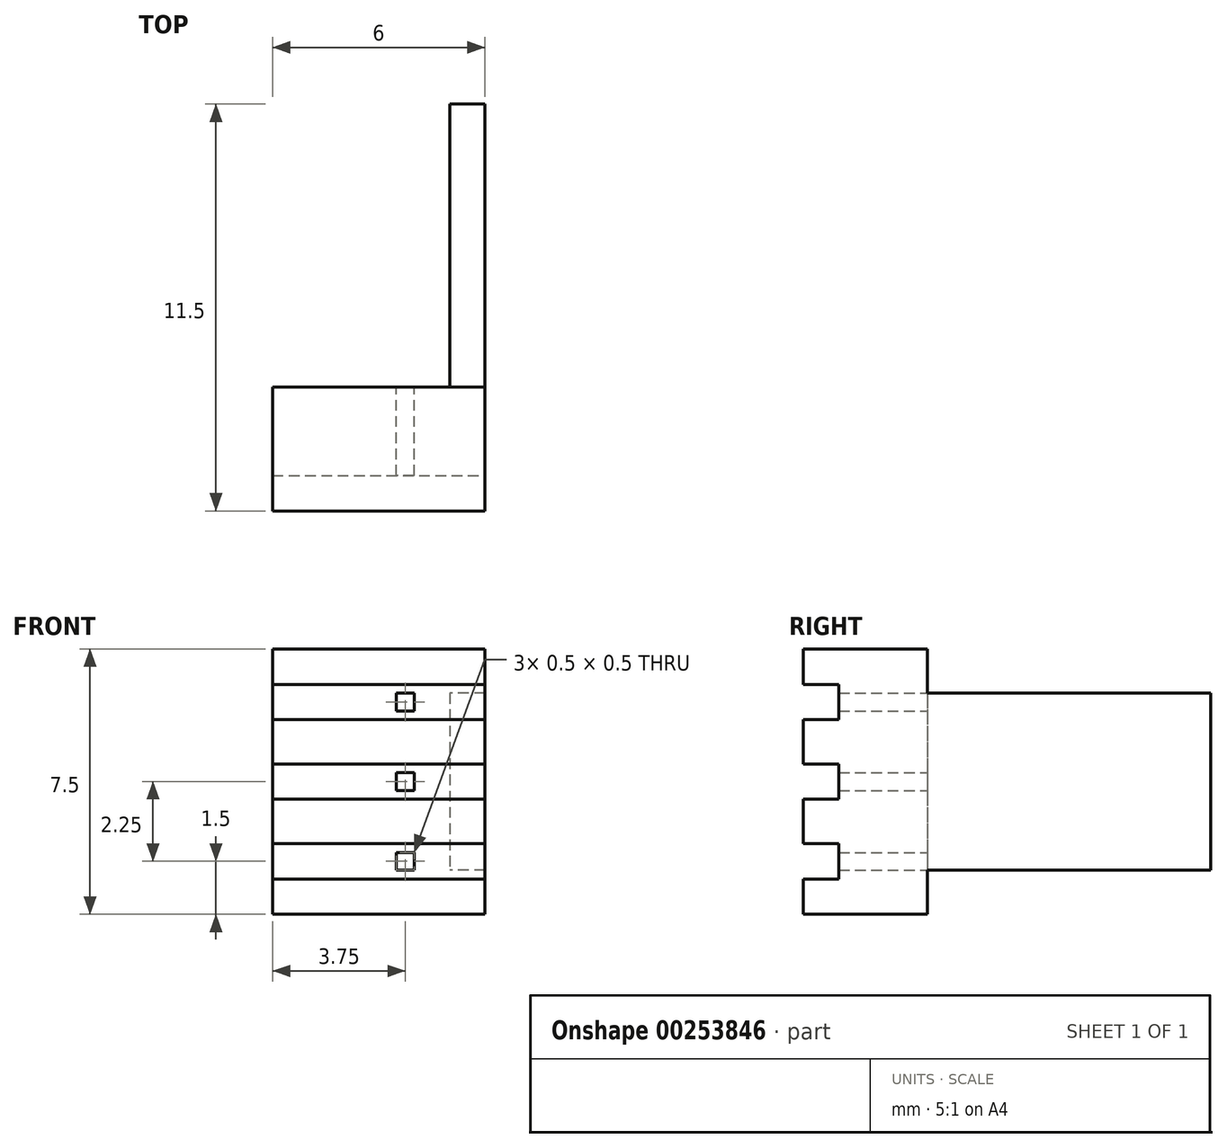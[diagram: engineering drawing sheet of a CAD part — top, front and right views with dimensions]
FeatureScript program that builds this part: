
annotation { "Feature Type Name" : "Feature", "Feature Type Description" : "" }
export const myFeature = defineFeature(function(context is Context, id is Id, definition is map)
    precondition{}
    {
        {
            var Q0;
            Q0=qCreatedBy(makeId("Top.planeOp"),FACE);
            var sketch = newSketch(context, id + "F0", { "sketchPlane" : qUnion([Q0])});
            skLineSegment(sketch, "E0.bottom", {"start": v(0, 0) * mm, "end": v(6, 0) * mm});
            skLineSegment(sketch, "E0.top", {"start": v(5, 11.5) * mm, "end": v(6, 11.5) * mm});
            skLineSegment(sketch, "E0.left", {"start": v(0, 0) * mm, "end": v(0, 3.5) * mm});
            skLineSegment(sketch, "E0.right", {"start": v(6, 0) * mm, "end": v(6, 11.5) * mm});
            skLineSegment(sketch, "E1", {"start": v(5, 11.5) * mm, "end": v(5, 3.5) * mm});
            skLineSegment(sketch, "E2", {"start": v(5, 3.5) * mm, "end": v(0, 3.5) * mm});
            skSolve(sketch);
        }
        {
            var Q0;
            Q0=qSketchRegion(id+"F0",true);
            extrude(context, id + "F1", {"entities" : qUnion([Q0]), "depth" : 7.5 * mm});
        }
        {
            var Q0;
            Q0=makeQuery(id+"F1.opExtrude","SWEPT_FACE",FACE,{"disambiguationData":[OSD([sQuery(id+"F0.wireOp",EDGE,"E1")])]});
            var sketch = newSketch(context, id + "F2", { "sketchPlane" : qUnion([Q0])});
            skLineSegment(sketch, "E3.bottom", {"start": v(-11.5, 0) * mm, "end": v(-3.5, 0) * mm});
            skLineSegment(sketch, "E3.top", {"start": v(-11.5, 1.25) * mm, "end": v(-3.5, 1.25) * mm});
            skLineSegment(sketch, "E3.left", {"start": v(-11.5, 0) * mm, "end": v(-11.5, 1.25) * mm});
            skLineSegment(sketch, "E3.right", {"start": v(-3.5, 0) * mm, "end": v(-3.5, 1.25) * mm});
            skLineSegment(sketch, "E4.bottom", {"start": v(-11.5, 7.5) * mm, "end": v(-3.5, 7.5) * mm});
            skLineSegment(sketch, "E4.top", {"start": v(-11.5, 6.25) * mm, "end": v(-3.5, 6.25) * mm});
            skLineSegment(sketch, "E4.left", {"start": v(-11.5, 7.5) * mm, "end": v(-11.5, 6.25) * mm});
            skLineSegment(sketch, "E4.right", {"start": v(-3.5, 7.5) * mm, "end": v(-3.5, 6.25) * mm});
            skSolve(sketch);
        }
        {
            var Q0;
            Q0=qSketchRegion(id+"F2",true);
            extrude(context, id + "F3", {"entities" : qUnion([Q0]), "operationType" : NewBodyOperationType.REMOVE, "oppositeDirection" : true, "depth" : 25 * mm});
        }
        {
            var Q0;
            Q0=makeQuery(id+"F3.boolean.opBoolean","MERGE",FACE,{"derivedFrom":[makeQuery(id+"F1.opExtrude","SWEPT_FACE",FACE,{"disambiguationData":[OSD([sQuery(id+"F0.wireOp",EDGE,"E2")])]}),makeQuery(id+"F3.opExtrude","SWEPT_FACE",FACE,{"disambiguationData":[OSD([sQuery(id+"F2.wireOp",EDGE,"E3.right")])]}),makeQuery(id+"F3.opExtrude","SWEPT_FACE",FACE,{"disambiguationData":[OSD([sQuery(id+"F2.wireOp",EDGE,"E4.right")])]})]});
            var sketch = newSketch(context, id + "F4", { "sketchPlane" : qUnion([Q0])});
            skLineSegment(sketch, "E5.bottom", {"start": v(-4, 6.25) * mm, "end": v(-3.5, 6.25) * mm});
            skLineSegment(sketch, "E5.top", {"start": v(-4, 1.25) * mm, "end": v(-3.5, 1.25) * mm});
            skLineSegment(sketch, "E5.left", {"start": v(-4, 6.25) * mm, "end": v(-4, 5.75) * mm});
            skLineSegment(sketch, "E5.right", {"start": v(-3.5, 6.25) * mm, "end": v(-3.5, 5.75) * mm});
            skLineSegment(sketch, "E6", {"start": v(-4, 5.75) * mm, "end": v(-3.5, 5.75) * mm});
            skLineSegment(sketch, "E7", {"start": v(-4, 1.75) * mm, "end": v(-3.5, 1.75) * mm});
            skLineSegment(sketch, "E8", {"start": v(-4, 4) * mm, "end": v(-3.5, 4) * mm});
            skLineSegment(sketch, "E9", {"start": v(-4, 3.5) * mm, "end": v(-3.5, 3.5) * mm});
            skLineSegment(sketch, "E10.trimOffspring", {"start": v(-4, 4) * mm, "end": v(-4, 3.5) * mm});
            skLineSegment(sketch, "E11.trimOffspring", {"start": v(-3.5, 4) * mm, "end": v(-3.5, 3.5) * mm});
            skLineSegment(sketch, "E12.trimOffspring", {"start": v(-4, 1.75) * mm, "end": v(-4, 1.25) * mm});
            skLineSegment(sketch, "E13.trimOffspring", {"start": v(-3.5, 1.75) * mm, "end": v(-3.5, 1.25) * mm});
            skLineSegment(sketch, "E14", {"start": v(0, 3.75) * mm, "end": v(-5, 3.75) * mm, "construction": true});
            skPoint(sketch, "E14.endSnap0", {"position": v(0, 3.75) * mm});
            skSolve(sketch);
        }
        {
            var Q0;
            Q0=qSketchRegion(id+"F4",true);
            var Q1;
            Q1=makeQuery(id+"F1.opExtrude","SWEPT_FACE",FACE,{"disambiguationData":[OSD([sQuery(id+"F0.wireOp",EDGE,"E0.top")])]});
            extrude(context, id + "F5", {"entities" : qUnion([Q0]), "operationType" : NewBodyOperationType.REMOVE, "oppositeDirection" : true, "endBoundEntityFace" : qUnion([Q1]), "depth" : 25 * mm});
        }
        {
            var Q0;
            Q0=makeQuery(id+"F1.opExtrude","SWEPT_FACE",FACE,{"disambiguationData":[OSD([sQuery(id+"F0.wireOp",EDGE,"E0.bottom")])]});
            var sketch = newSketch(context, id + "F6", { "sketchPlane" : qUnion([Q0])});
            skLineSegment(sketch, "E15.bottom", {"start": v(0, 6.5) * mm, "end": v(6, 6.5) * mm});
            skLineSegment(sketch, "E15.top", {"start": v(0, 5.5) * mm, "end": v(6, 5.5) * mm});
            skLineSegment(sketch, "E15.left", {"start": v(0, 6.5) * mm, "end": v(0, 5.5) * mm});
            skLineSegment(sketch, "E15.right", {"start": v(6, 6.5) * mm, "end": v(6, 5.5) * mm});
            skLineSegment(sketch, "E16.bottom", {"start": v(0, 4.25) * mm, "end": v(6, 4.25) * mm});
            skLineSegment(sketch, "E16.top", {"start": v(0, 3.25) * mm, "end": v(6, 3.25) * mm});
            skLineSegment(sketch, "E16.left", {"start": v(0, 4.25) * mm, "end": v(0, 3.25) * mm});
            skLineSegment(sketch, "E16.right", {"start": v(6, 4.25) * mm, "end": v(6, 3.25) * mm});
            skLineSegment(sketch, "E17.bottom", {"start": v(0, 2) * mm, "end": v(6, 2) * mm});
            skLineSegment(sketch, "E17.top", {"start": v(0, 1) * mm, "end": v(6, 1) * mm});
            skLineSegment(sketch, "E17.left", {"start": v(0, 2) * mm, "end": v(0, 1) * mm});
            skLineSegment(sketch, "E17.right", {"start": v(6, 2) * mm, "end": v(6, 1) * mm});
            skSolve(sketch);
        }
        {
            var Q0;
            Q0 = qSketchRegion(id + "F6", true);
            extrude(context, id + "F7", {"entities" : qUnion([Q0]), "operationType" : NewBodyOperationType.REMOVE, "oppositeDirection" : true, "depth" : 1 * mm});
        }
    });
